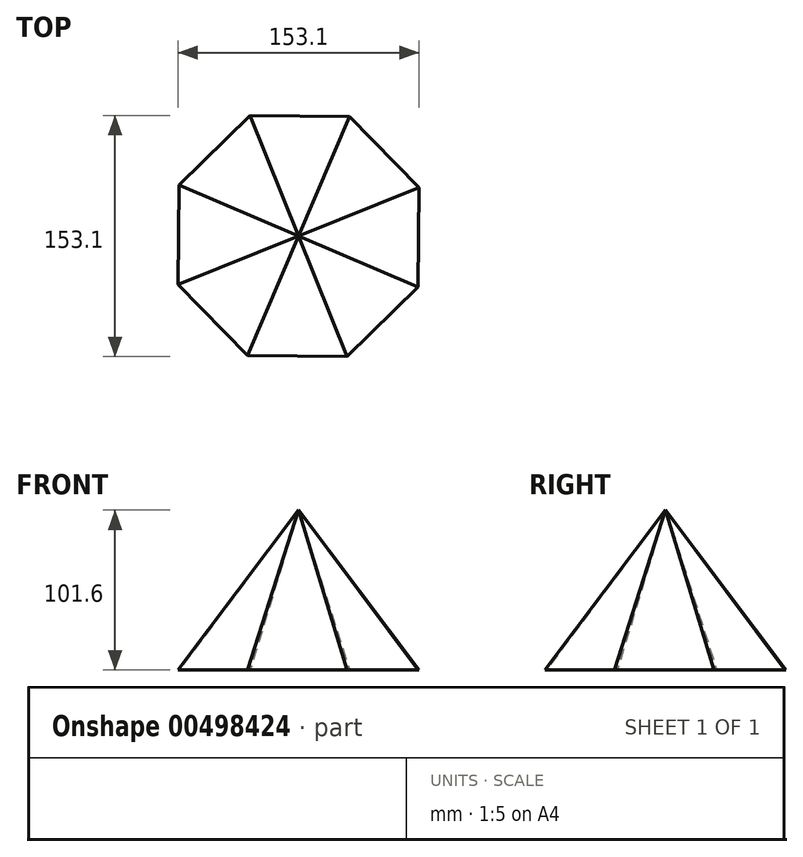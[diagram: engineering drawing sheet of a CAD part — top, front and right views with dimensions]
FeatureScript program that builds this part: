
annotation { "Feature Type Name" : "Feature", "Feature Type Description" : "" }
export const myFeature = defineFeature(function(context is Context, id is Id, definition is map)
    precondition{}
    {
        {
            var Q0;
            Q0=qCreatedBy(makeId("Top.planeOp"),FACE);
            var sketch = newSketch(context, id + "F0", { "sketchPlane" : qUnion([Q0])});
            skCircle(sketch, "E0.cCircle", {"center": v(0, 0) * mm, "radius": 82.48 * mm, "construction": true});
            skLineSegment(sketch, "E0.0", {"start": v(32.42, 75.84) * mm, "end": v(76.55, 30.7) * mm});
            skLineSegment(sketch, "E0.1", {"start": v(76.55, 30.7) * mm, "end": v(75.84, -32.42) * mm});
            skLineSegment(sketch, "E0.2", {"start": v(75.84, -32.42) * mm, "end": v(30.7, -76.55) * mm});
            skLineSegment(sketch, "E0.3", {"start": v(30.7, -76.55) * mm, "end": v(-32.42, -75.84) * mm});
            skLineSegment(sketch, "E0.4", {"start": v(-32.42, -75.84) * mm, "end": v(-76.55, -30.7) * mm});
            skLineSegment(sketch, "E0.5", {"start": v(-76.55, -30.7) * mm, "end": v(-75.84, 32.42) * mm});
            skLineSegment(sketch, "E0.6", {"start": v(-75.84, 32.42) * mm, "end": v(-30.7, 76.55) * mm});
            skLineSegment(sketch, "E0.7", {"start": v(-30.7, 76.55) * mm, "end": v(32.42, 75.84) * mm});
            skSolve(sketch);
        }
        {
            var Q0;
            Q0=qCreatedBy(makeId("Top.planeOp"),FACE);
            cPlane(context, id + "F1", {"entities" : qUnion([Q0]), "cplaneType" : CPlaneType.OFFSET, "offset" : 101.6 * mm, "width" : 152.4 * mm, "height" : 152.4 * mm});
        }
        {
            var Q0;
            Q0=qCreatedBy(id+"F1.planeOp",FACE);
            var sketch = newSketch(context, id + "F2", { "sketchPlane" : qUnion([Q0])});
            skPoint(sketch, "E1", {"position": v(0, 0) * mm});
            skSolve(sketch);
        }
        {
            var Q0;
            Q0=sQuery(id+"F2.wireOp",VERTEX,"E1");
            var Q1;
            Q1=makeQuery(id+"F0.imprint","IMPRINT",FACE,{"disambiguationData":[TD([[makeQuery(id+"F0.imprint","IMPRINT",EDGE,{"derivedFrom":sQuery(id+"F0.wireOp",EDGE,"E0.0")}),-1.0]])]});
            loft(context, id + "F3", {"sheetProfilesArray" : [{ "sheetProfileEntities" : qUnion([Q0]) }, { "sheetProfileEntities" : qUnion([Q1]) }]});
        }
    });
